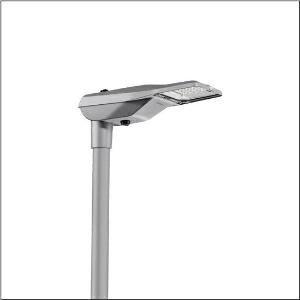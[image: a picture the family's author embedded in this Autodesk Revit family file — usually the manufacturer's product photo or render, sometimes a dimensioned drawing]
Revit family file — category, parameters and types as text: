
# Revit family: streetlight_sl_21_micro___pl52_5xe1h43t08db_9fac
name_source: partatom
category: Lighting Fixtures
units: mm (PartAtom-declared; Revit-internal decimal feet)

## family parameters
Cut with Voids When Loaded = No
Host = Face
Light Source = No
Part Type = Normal
Room Calculation Point = No
Round Connector Dimension = Use Diameter
Shared = No

## types (1)
- --- (1 x LED, 5230 lm, 39.1 W, 4000K)
    Apparent Load = 39 VA
    CIE Flux Codes = 27 59 98 100 100
    Color Rendering = 70
    Color Temperature = 4000K
    Default Elevation = 1800 mm
    Description = Streetlight SL 21 micro, mast luminaire, primary light control with lens, of PMMA, primary optical cover: cover, of toughened safety glass, transparent, light distribution: PL52, light emission: direct distribution, primary light characteristic: asymmetric, installation type: side-entry, post-top, LED, High Power LED, rated luminous flux: 5.230lm, luminous efficacy: 134lm/W, light colour: 740, colour temperature: 4000K, control: flexible luminous flux parameterisation, time-dependent luminous flux control, constant luminous flux control, overheat protection, presetting dimming logarithmic, mains connection: 220..240V, AC, 50/60Hz, start of lifetime: 39W, end of service life: 41W, reduction: 18W, luminaire housing, of diecast aluminium, powder-coated, Siteco® metallic grey (DB 702S), corrosivity category C5 mid according to DIN EN ISO 12944, please order mast flange separately, inclination adjustable: 0°, 5°, 10°, 15°, sealing non-destructively replaceable, multi-level sealing system, length: 528mm, width: 235mm, height: 110mm, mast flange for spigot size: 42mm (side-entry): 5XC10008XM4, 60/48mm (side-entry/post-top): 5XC10108XM2, 76/60mm (side-entry/post-top): 5XC10108XM1, Smart Interface below and above, protection rating (complete): IP66, insulation class (complete): insulation class II (safety insulation), certification: CE, ENEC, ENEC+, VDE, impact resistance: IK09, permissible operating ambient temperature for outdoor applications: -40..+50°C, standard-compliant lighting for roads and squares, packaging unit: 1 piece

Light Distribution: PL52
    Height = 110 mm
    Lamp = 1 x LED
    Lamp Light Flux = 5230 lm
    Lamp Power = 39.1 W
    Lamp count = 1
    Length = 528 mm
    Luminous efficacy = 134 lm/W
    Manufacturer = Siteco
    ModVariant = No
    Model = 5XE1H43T08DB
    Number of Poles = 1
    OnlyDefault = Yes
    Power Factor = 1
    Product Name = Streetlight SL 21 micro | PL52
    Product group = mast luminaire | pylon top
    ProductGroupID = 6100
    Protection Class = Protection class II
    Protection Degree = IP 66
    RLX_Detail_Level = 1
    RLX_Emergency_Light_Flux = 0 lm
    RLX_Emergency_Type = 0
    RLX_Emergency_Type_DB = No
    RlxData = <blob elided: 107765 chars, md5=e250a042>
    Socket = socket
    Standby Power = 0 W
    System Light Flux = 5230 lm
    System Power = 39 W
    Type Comments = factory setting: luminous flux: 100 % | dim-lin: 254 | 765 mA
    Type Image = l_1007239.jpg
    URL = http://relux.com
    VarID = @adj_106291
    Voltage = 0 V
    Weight = 0.00 kg
    Width = 235 mm

## geometry (parser evidence)
native form markers: Blend x4, Sweep x10
no freeform markers — native parametric forms only
